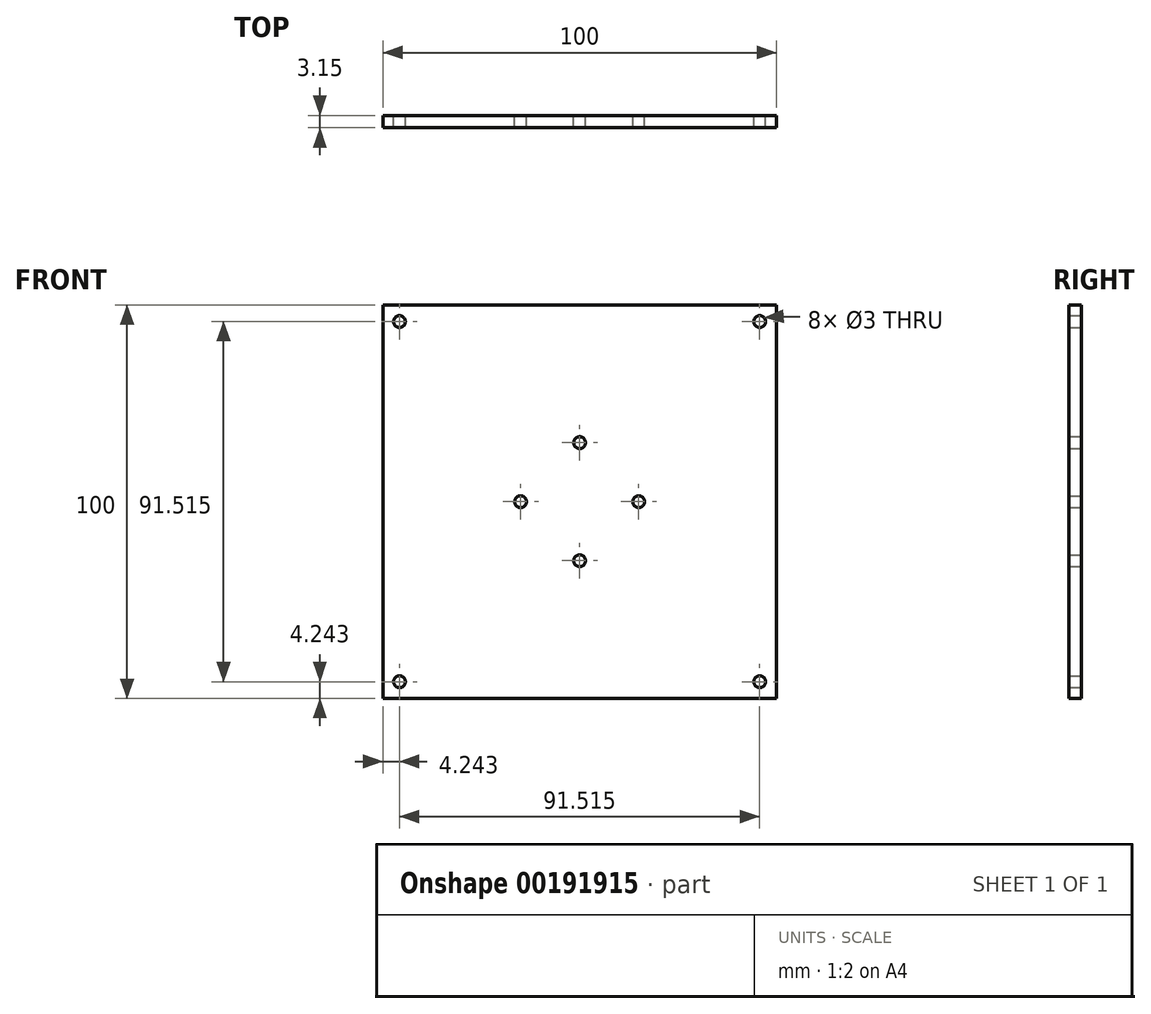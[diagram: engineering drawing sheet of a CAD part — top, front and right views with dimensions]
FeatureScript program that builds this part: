
annotation { "Feature Type Name" : "Feature", "Feature Type Description" : "" }
export const myFeature = defineFeature(function(context is Context, id is Id, definition is map)
    precondition{}
    {
        {
            var Q0;
            Q0=qCreatedBy(makeId("Front.planeOp"),FACE);
            var sketch = newSketch(context, id + "F0", { "sketchPlane" : qUnion([Q0])});
            skLineSegment(sketch, "E0.bottom", {"start": v(50, 50) * mm, "end": v(-50, 50) * mm});
            skLineSegment(sketch, "E0.top", {"start": v(50, -50) * mm, "end": v(-50, -50) * mm});
            skLineSegment(sketch, "E0.left", {"start": v(50, 50) * mm, "end": v(50, -50) * mm});
            skLineSegment(sketch, "E0.right", {"start": v(-50, 50) * mm, "end": v(-50, -50) * mm});
            skPoint(sketch, "E0.middle", {"position": v(0, 0) * mm});
            skCircle(sketch, "E1", {"center": v(0, 0) * mm, "radius": 15 * mm, "construction": true});
            skCircle(sketch, "E2", {"center": v(0, 15) * mm, "radius": 1.5 * mm});
            skCircle(sketch, "E3.1.0", {"center": v(-15, 0) * mm, "radius": 1.5 * mm});
            skCircle(sketch, "E3.2.0", {"center": v(0, -15) * mm, "radius": 1.5 * mm});
            skCircle(sketch, "E3.3.0", {"center": v(15, 0) * mm, "radius": 1.5 * mm});
            skLineSegment(sketch, "E4", {"start": v(-50, -50) * mm, "end": v(50, 50) * mm, "construction": true});
            skLineSegment(sketch, "E5", {"start": v(-50, 50) * mm, "end": v(50, -50) * mm, "construction": true});
            skCircle(sketch, "E6", {"center": v(45.76, 45.76) * mm, "radius": 1.5 * mm});
            skCircle(sketch, "E7", {"center": v(-45.76, 45.76) * mm, "radius": 1.5 * mm});
            skCircle(sketch, "E8", {"center": v(-45.76, -45.76) * mm, "radius": 1.5 * mm});
            skCircle(sketch, "E9", {"center": v(45.76, -45.76) * mm, "radius": 1.5 * mm});
            skSolve(sketch);
        }
        {
            var Q0;
            Q0=makeQuery(id+"F0.imprint","IMPRINT",FACE,{"disambiguationData":[TD([[makeQuery(id+"F0.imprint","IMPRINT",EDGE,{"derivedFrom":sQuery(id+"F0.wireOp",EDGE,"E0.bottom")}),1.0]])]});
            extrude(context, id + "F1", {"entities" : qUnion([Q0]), "depth" : 3.15 * mm});
        }
    });
